# Revit family: DCS_Revit_18_BE1-36RC-N_or_L_Grill_90000782A
name_source: partatom
category: Specialty Equipment
revit_build: Autodesk Revit 2018 (Build: 20170223_1515(x64)
units: mm (PartAtom-declared; Revit-internal decimal feet)

## family parameters
Always vertical = Yes
Cut with Voids When Loaded = Yes
OmniClass Number = 23.40.40.14.17.27
OmniClass Title = Barbecues
Part Type = Normal
Room Calculation Point = No
Round Connector Dimension = Use Diameter
Shared = No
Work Plane-Based = No

## types (2) — shared parameters
Clearance - Below Combustible = 457 mm  [stored 1.49934 ft]
Clearance - Overhead Non-Combustible = 670 mm  [stored 2.19816 ft]
Clearance - Rear Combustible = 457 mm  [stored 1.49934 ft]
Clearance - Rear Non-Combustible = 76 mm  [stored 0.249344 ft]
Clearance - Side Combustible = 457 mm  [stored 1.49934 ft]
Clearance - Side Non-Combustible = 76 mm  [stored 0.249344 ft]
Connector Description - Electrical = 120 V, 15A, GFI electrical outlet
Connector Description - Gas = Operating Pressure NG 4” WC, LPG 11” WC, Connection is 1/2” NPT female
Manufacturer = Fisher & Paykel Appliances
Material - Body = DCS - Stainless Steel
Material - Handle = DCS - Aluminium
Material - Trim = DCS - Steel, Chrome Plated
URL = www.dcsappliances.com
Visibility - Clearance Required = Yes

## per-type parameters (varying)
| type | Cavity - Depth | Cavity - Height | Cavity - Width | Description | Model | Product - Depth | Product - Height | Product - Width | Visibility - Clearance Required (Below Countertop) | Visibility - Insulation Jacket |
| Grill | 578 mm  [stored 1.89633 ft] | 257 mm  [stored 0.843176 ft] | 876 mm  [stored 2.87402 ft] | DCS 36" Series 9 Evolution Grill | BE1-36RC-N or BE1-36RC-L | 695 mm  [stored 2.28018 ft] | 698 mm  [stored 2.29003 ft] | 913 mm | Yes | No |
| Grill with Insulated Jacket | 603 mm | 283 mm  [stored 0.928478 ft] | 1029 mm  [stored 3.37598 ft] | DCS 36" Series 9 Evolution Grill with 36" Insulated Jacket | BE1-36RC-N or BE1-36RC-L with BGA36-IJS | 706 mm  [stored 2.31627 ft] | 726 mm  [stored 2.38189 ft] | 1026 mm  [stored 3.36614 ft] | No | Yes |

note: [stored X ft] marks values corroborated as IEEE doubles in the binary element streams (Revit-internal decimal feet)

## geometry (parser evidence)
native form markers: Sweep x20
no freeform markers — native parametric forms only
